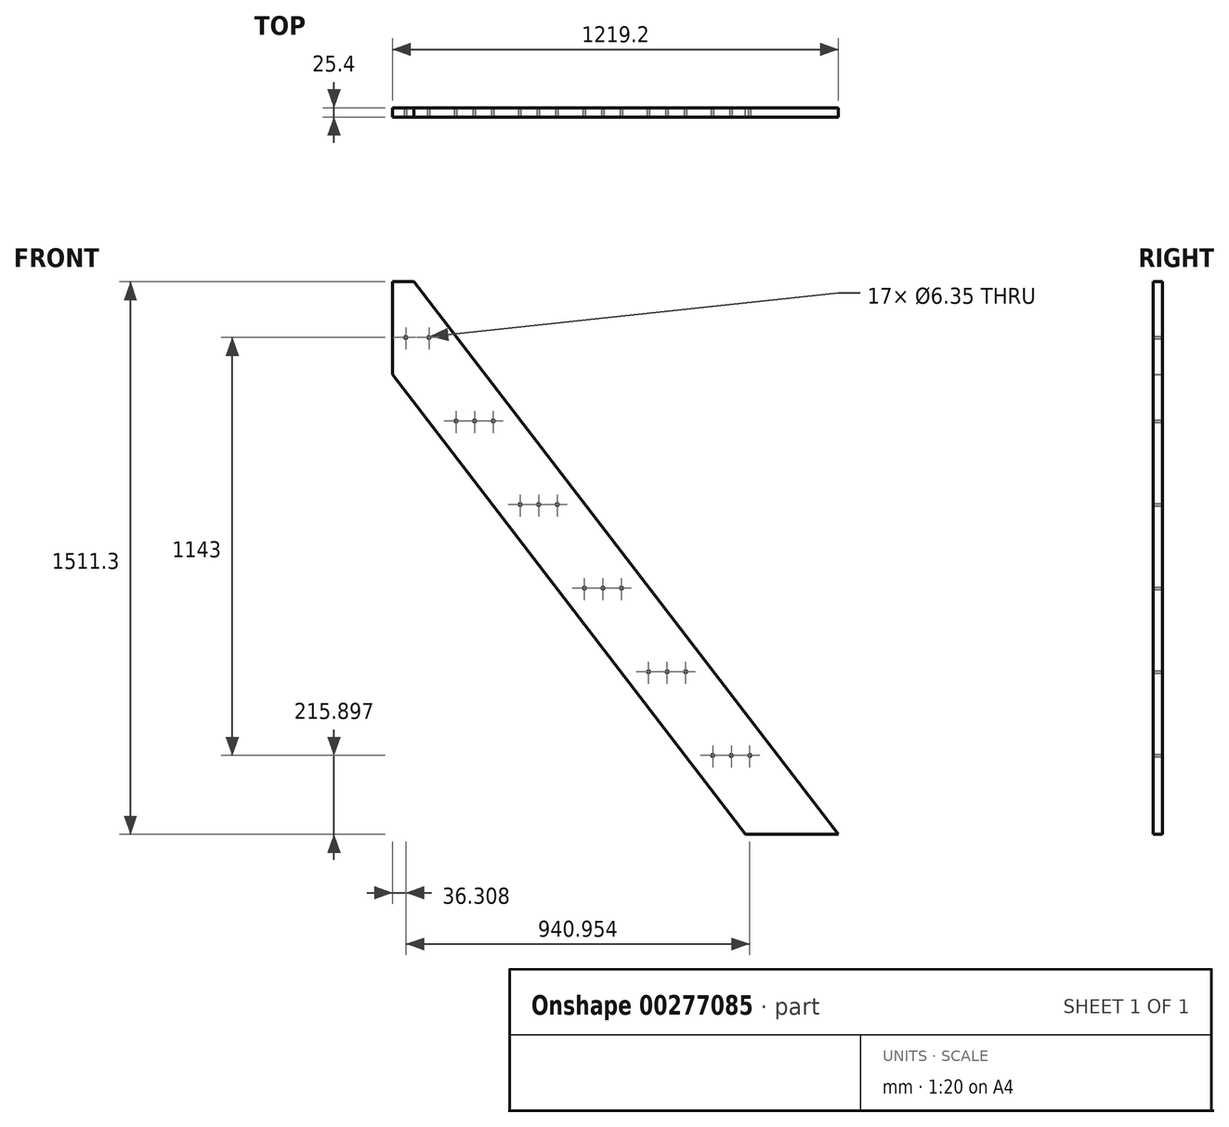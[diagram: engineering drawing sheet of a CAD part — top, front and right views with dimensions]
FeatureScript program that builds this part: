
annotation { "Feature Type Name" : "Feature", "Feature Type Description" : "" }
export const myFeature = defineFeature(function(context is Context, id is Id, definition is map)
    precondition{}
    {
        {
            var Q0;
            Q0=qCreatedBy(makeId("Front.planeOp"),FACE);
            var sketch = newSketch(context, id + "F0", { "sketchPlane" : qUnion([Q0])});
            skLineSegment(sketch, "E0", {"start": v(1730.25, -1410.8) * mm, "end": v(1476.25, -1410.8) * mm});
            skLineSegment(sketch, "E1", {"start": v(1476.25, -1410.8) * mm, "end": v(511.05, -153.5) * mm});
            skLineSegment(sketch, "E2", {"start": v(511.05, -153.5) * mm, "end": v(511.05, 100.5) * mm});
            skLineSegment(sketch, "E3", {"start": v(511.05, 100.5) * mm, "end": v(570.06, 100.5) * mm});
            skLineSegment(sketch, "E4", {"start": v(570.06, 100.5) * mm, "end": v(1730.25, -1410.8) * mm});
            skCircle(sketch, "E5", {"center": v(1386.71, -1194.9) * mm, "radius": 3.18 * mm});
            skCircle(sketch, "E6", {"center": v(1488.31, -1194.9) * mm, "radius": 3.18 * mm});
            skCircle(sketch, "E7", {"center": v(1437.51, -1194.9) * mm, "radius": 3.18 * mm});
            skCircle(sketch, "E8", {"center": v(1211.22, -966.3) * mm, "radius": 3.18 * mm});
            skCircle(sketch, "E9", {"center": v(1262.02, -966.3) * mm, "radius": 3.18 * mm});
            skCircle(sketch, "E10", {"center": v(1312.82, -966.3) * mm, "radius": 3.18 * mm});
            skCircle(sketch, "E11", {"center": v(1137.33, -737.7) * mm, "radius": 3.18 * mm});
            skCircle(sketch, "E12", {"center": v(1086.53, -737.7) * mm, "radius": 3.18 * mm});
            skCircle(sketch, "E13", {"center": v(1035.73, -737.7) * mm, "radius": 3.18 * mm});
            skCircle(sketch, "E14", {"center": v(961.84, -509.1) * mm, "radius": 3.18 * mm});
            skCircle(sketch, "E15", {"center": v(911.04, -509.1) * mm, "radius": 3.18 * mm});
            skCircle(sketch, "E16", {"center": v(860.24, -509.1) * mm, "radius": 3.18 * mm});
            skCircle(sketch, "E17", {"center": v(786.35, -280.5) * mm, "radius": 3.18 * mm});
            skCircle(sketch, "E18", {"center": v(735.55, -280.5) * mm, "radius": 3.18 * mm});
            skCircle(sketch, "E19", {"center": v(684.75, -280.5) * mm, "radius": 3.18 * mm});
            skCircle(sketch, "E20", {"center": v(547.36, -51.9) * mm, "radius": 3.18 * mm});
            skCircle(sketch, "E21", {"center": v(610.86, -51.9) * mm, "radius": 3.18 * mm});
            skLineSegment(sketch, "E22.bottom", {"start": v(521.96, -64.6) * mm, "end": v(636.26, -64.6) * mm, "construction": true});
            skLineSegment(sketch, "E22.top", {"start": v(521.96, -39.2) * mm, "end": v(636.26, -39.2) * mm, "construction": true});
            skLineSegment(sketch, "E22.left", {"start": v(521.96, -64.6) * mm, "end": v(521.96, -39.2) * mm, "construction": true});
            skLineSegment(sketch, "E22.right", {"start": v(636.26, -64.6) * mm, "end": v(636.26, -39.2) * mm, "construction": true});
            skLineSegment(sketch, "E23.bottom", {"start": v(659.35, -293.2) * mm, "end": v(811.75, -293.2) * mm, "construction": true});
            skLineSegment(sketch, "E23.top", {"start": v(659.35, -267.8) * mm, "end": v(811.75, -267.8) * mm, "construction": true});
            skLineSegment(sketch, "E23.left", {"start": v(659.35, -293.2) * mm, "end": v(659.35, -267.8) * mm, "construction": true});
            skLineSegment(sketch, "E23.right", {"start": v(811.75, -293.2) * mm, "end": v(811.75, -267.8) * mm, "construction": true});
            skLineSegment(sketch, "E24.bottom", {"start": v(834.84, -521.8) * mm, "end": v(987.24, -521.8) * mm, "construction": true});
            skLineSegment(sketch, "E24.top", {"start": v(834.84, -496.4) * mm, "end": v(987.24, -496.4) * mm, "construction": true});
            skLineSegment(sketch, "E24.left", {"start": v(834.84, -521.8) * mm, "end": v(834.84, -496.4) * mm, "construction": true});
            skLineSegment(sketch, "E24.right", {"start": v(987.24, -521.8) * mm, "end": v(987.24, -496.4) * mm, "construction": true});
            skLineSegment(sketch, "E25.bottom", {"start": v(1010.33, -750.4) * mm, "end": v(1162.73, -750.4) * mm, "construction": true});
            skLineSegment(sketch, "E25.top", {"start": v(1010.33, -725) * mm, "end": v(1162.73, -725) * mm, "construction": true});
            skLineSegment(sketch, "E25.left", {"start": v(1010.33, -750.4) * mm, "end": v(1010.33, -725) * mm, "construction": true});
            skLineSegment(sketch, "E25.right", {"start": v(1162.73, -750.4) * mm, "end": v(1162.73, -725) * mm, "construction": true});
            skLineSegment(sketch, "E26.bottom", {"start": v(1185.08, -979) * mm, "end": v(1337.48, -979) * mm, "construction": true});
            skLineSegment(sketch, "E26.top", {"start": v(1185.08, -953.6) * mm, "end": v(1337.48, -953.6) * mm, "construction": true});
            skLineSegment(sketch, "E26.left", {"start": v(1185.08, -979) * mm, "end": v(1185.08, -953.6) * mm, "construction": true});
            skLineSegment(sketch, "E26.right", {"start": v(1337.48, -979) * mm, "end": v(1337.48, -953.6) * mm, "construction": true});
            skLineSegment(sketch, "E27.bottom", {"start": v(1361.31, -1207.6) * mm, "end": v(1513.71, -1207.6) * mm, "construction": true});
            skLineSegment(sketch, "E27.top", {"start": v(1361.31, -1182.2) * mm, "end": v(1513.71, -1182.2) * mm, "construction": true});
            skLineSegment(sketch, "E27.left", {"start": v(1361.31, -1207.6) * mm, "end": v(1361.31, -1182.2) * mm, "construction": true});
            skLineSegment(sketch, "E27.right", {"start": v(1513.71, -1207.6) * mm, "end": v(1513.71, -1182.2) * mm, "construction": true});
            skSolve(sketch);
        }
        {
            var Q0;
            Q0=makeQuery(id+"F0.imprint","IMPRINT",FACE,{"disambiguationData":[TD([[makeQuery(id+"F0.imprint","IMPRINT",EDGE,{"derivedFrom":sQuery(id+"F0.wireOp",EDGE,"E0")}),-1.0]])]});
            extrude(context, id + "F1", {"entities" : qUnion([Q0]), "depth" : 25.4 * mm});
        }
    });
